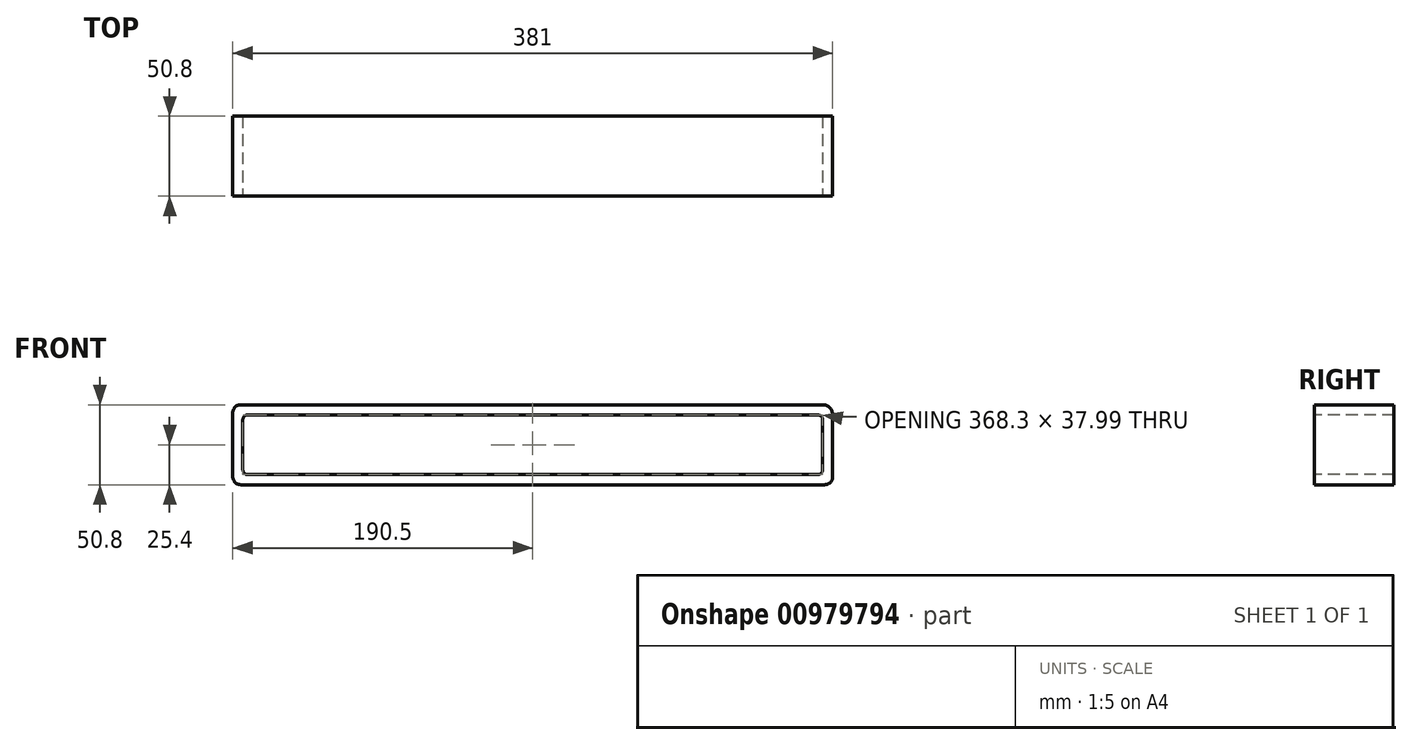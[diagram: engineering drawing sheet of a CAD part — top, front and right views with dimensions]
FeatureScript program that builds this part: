
annotation { "Feature Type Name" : "Feature", "Feature Type Description" : "" }
export const myFeature = defineFeature(function(context is Context, id is Id, definition is map)
    precondition{}
    {
        {
            var Q0;
            Q0=qCreatedBy(makeId("Front.planeOp"),FACE);
            var sketch = newSketch(context, id + "F0", { "sketchPlane" : qUnion([Q0])});
            skLineSegment(sketch, "E0.bottom", {"start": v(190.5, -25.4) * mm, "end": v(-190.5, -25.4) * mm});
            skLineSegment(sketch, "E0.top", {"start": v(190.5, 25.4) * mm, "end": v(-190.5, 25.4) * mm});
            skLineSegment(sketch, "E0.left", {"start": v(190.5, -25.4) * mm, "end": v(190.5, 25.4) * mm});
            skLineSegment(sketch, "E0.right", {"start": v(-190.5, -25.4) * mm, "end": v(-190.5, 25.4) * mm});
            skPoint(sketch, "E0.middle", {"position": v(0, 0) * mm});
            skSolve(sketch);
        }
        {
            var Q0;
            Q0=makeQuery(id+"F0.imprint","IMPRINT",FACE,{"disambiguationData":[TD([[makeQuery(id+"F0.imprint","IMPRINT",EDGE,{"derivedFrom":sQuery(id+"F0.wireOp",EDGE,"E0.bottom")}),-1.0]])]});
            extrude(context, id + "F1", {"entities" : qUnion([Q0]), "depth" : 50.8 * mm, "offsetDistance" : 25.4 * mm});
        }
        {
            var Q0;
            Q0=makeQuery(id+"F1.opExtrude","SWEPT_EDGE",EDGE,{"disambiguationData":[OSD([sQuery(id+"F0.wireOp",EDGE,"E0.top"),sQuery(id+"F0.wireOp",EDGE,"E0.left")])]});
            fillet(context, id + "F2", {"entities" : qUnion([Q0]), "radius" : 6.35 * mm, "tangentPropagation" : true, "allowEdgeOverflow" : false});
        }
        {
            var Q0;
            Q0=makeQuery(id+"F1.opExtrude","SWEPT_EDGE",EDGE,{"disambiguationData":[OSD([sQuery(id+"F0.wireOp",EDGE,"E0.bottom"),sQuery(id+"F0.wireOp",EDGE,"E0.left")])]});
            var Q1;
            Q1=makeQuery(id+"F1.opExtrude","SWEPT_EDGE",EDGE,{"disambiguationData":[OSD([sQuery(id+"F0.wireOp",EDGE,"E0.top"),sQuery(id+"F0.wireOp",EDGE,"E0.right")])]});
            var Q2;
            Q2=makeQuery(id+"F1.opExtrude","SWEPT_EDGE",EDGE,{"disambiguationData":[OSD([sQuery(id+"F0.wireOp",EDGE,"E0.bottom"),sQuery(id+"F0.wireOp",EDGE,"E0.right")])]});
            fillet(context, id + "F3", {"entities" : qUnion([Q0, Q1, Q2]), "radius" : 5.08 * mm, "tangentPropagation" : true, "allowEdgeOverflow" : false});
        }
        {
            var Q0;
            Q0=makeQuery(id+"F1.opExtrude","SWEPT_BODY",BODY,{"disambiguationData":[OSD([sQuery(id+"F0.wireOp",EDGE,"E0.bottom"),sQuery(id+"F0.wireOp",EDGE,"E0.top"),sQuery(id+"F0.wireOp",EDGE,"E0.left"),sQuery(id+"F0.wireOp",EDGE,"E0.right")])]});
            transform(context, id + "F4", {"entities" : qUnion([Q0]), "transformType" : TransformType.TRANSLATION_3D, "dx" : 0 * mm, "dy" : 50.8 * mm, "dz" : 0 * mm, "makeCopy" : false});
        }
        {
            var Q0;
            Q0=qCreatedBy(makeId("Front.planeOp"),FACE);
            var sketch = newSketch(context, id + "F5", { "sketchPlane" : qUnion([Q0])});
            skLineSegment(sketch, "E1.bottom", {"start": v(184.15, -19) * mm, "end": v(-184.15, -19) * mm});
            skLineSegment(sketch, "E1.top", {"start": v(184.15, 19) * mm, "end": v(-184.15, 19) * mm});
            skLineSegment(sketch, "E1.left", {"start": v(184.15, -19) * mm, "end": v(184.15, 19) * mm});
            skLineSegment(sketch, "E1.right", {"start": v(-184.15, -19) * mm, "end": v(-184.15, 19) * mm});
            skPoint(sketch, "E1.middle", {"position": v(0, 0) * mm});
            skSolve(sketch);
        }
        {
            var Q0;
            Q0=makeQuery(id+"F5.imprint","IMPRINT",FACE,{"disambiguationData":[TD([[makeQuery(id+"F5.imprint","IMPRINT",EDGE,{"derivedFrom":sQuery(id+"F5.wireOp",EDGE,"E1.bottom")}),-1.0]])]});
            extrude(context, id + "F6", {"entities" : qUnion([Q0]), "operationType" : NewBodyOperationType.REMOVE, "oppositeDirection" : true, "depth" : 50.8 * mm, "offsetDistance" : 25.4 * mm});
        }
        {
            var Q0;
            Q0=makeQuery(id+"F6.boolean.opBoolean","COPY",EDGE,{"derivedFrom":makeQuery(id+"F6.opExtrude","SWEPT_EDGE",EDGE,{"disambiguationData":[OSD([sQuery(id+"F5.wireOp",EDGE,"E1.bottom"),sQuery(id+"F5.wireOp",EDGE,"E1.left")])]})});
            var Q1;
            Q1=makeQuery(id+"F6.boolean.opBoolean","COPY",EDGE,{"derivedFrom":makeQuery(id+"F6.opExtrude","SWEPT_EDGE",EDGE,{"disambiguationData":[OSD([sQuery(id+"F5.wireOp",EDGE,"E1.top"),sQuery(id+"F5.wireOp",EDGE,"E1.left")])]})});
            var Q2;
            Q2=makeQuery(id+"F6.boolean.opBoolean","COPY",EDGE,{"derivedFrom":makeQuery(id+"F6.opExtrude","SWEPT_EDGE",EDGE,{"disambiguationData":[OSD([sQuery(id+"F5.wireOp",EDGE,"E1.top"),sQuery(id+"F5.wireOp",EDGE,"E1.right")])]})});
            var Q3;
            Q3=makeQuery(id+"F6.boolean.opBoolean","COPY",EDGE,{"derivedFrom":makeQuery(id+"F6.opExtrude","SWEPT_EDGE",EDGE,{"disambiguationData":[OSD([sQuery(id+"F5.wireOp",EDGE,"E1.bottom"),sQuery(id+"F5.wireOp",EDGE,"E1.right")])]})});
            fillet(context, id + "F7", {"entities" : qUnion([Q0, Q1, Q2, Q3]), "radius" : 3.17 * mm, "tangentPropagation" : true, "allowEdgeOverflow" : false});
        }
        {
            var Q0;
            Q0=makeQuery(id+"F1.opExtrude","SWEPT_BODY",BODY,{"disambiguationData":[OSD([sQuery(id+"F0.wireOp",EDGE,"E0.bottom"),sQuery(id+"F0.wireOp",EDGE,"E0.top"),sQuery(id+"F0.wireOp",EDGE,"E0.left"),sQuery(id+"F0.wireOp",EDGE,"E0.right")])]});
            transform(context, id + "F8", {"entities" : qUnion([Q0]), "transformType" : TransformType.TRANSLATION_3D, "dx" : 0 * mm, "dy" : 50.8 * mm, "dz" : 0 * mm, "makeCopy" : false});
        }
        {
            var Q0;
            Q0=makeQuery(id+"F1.opExtrude","SWEPT_BODY",BODY,{"disambiguationData":[OSD([sQuery(id+"F0.wireOp",EDGE,"E0.bottom"),sQuery(id+"F0.wireOp",EDGE,"E0.top"),sQuery(id+"F0.wireOp",EDGE,"E0.left"),sQuery(id+"F0.wireOp",EDGE,"E0.right")])]});
            transform(context, id + "F9", {"entities" : qUnion([Q0]), "transformType" : TransformType.TRANSLATION_3D, "dx" : 0 * mm, "dy" : 0 * mm, "dz" : -101.6 * mm, "makeCopy" : false});
        }
    });
